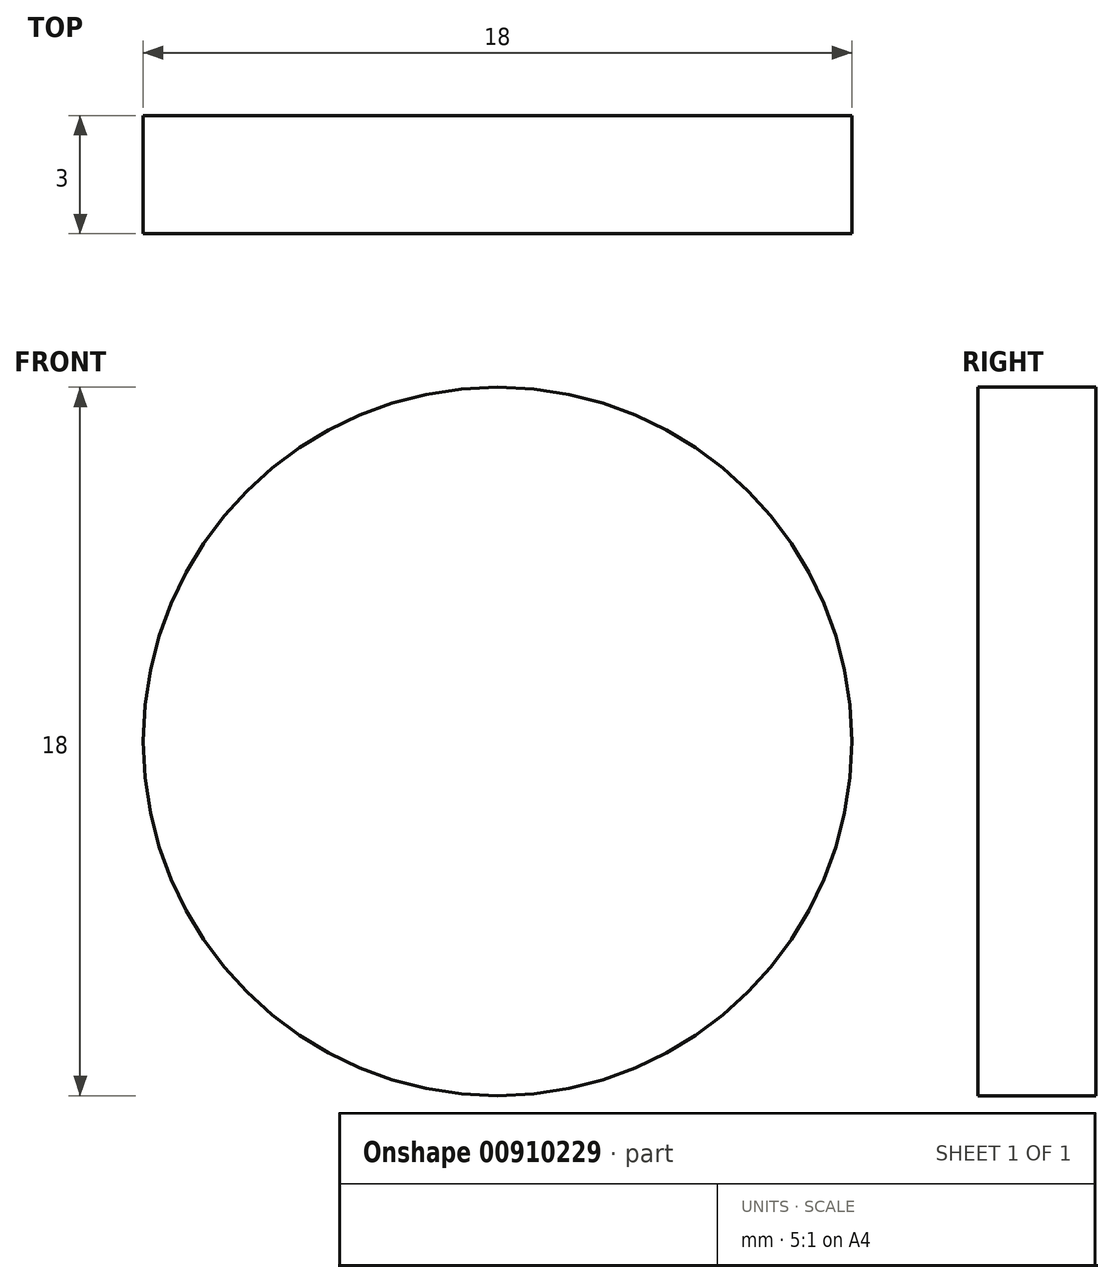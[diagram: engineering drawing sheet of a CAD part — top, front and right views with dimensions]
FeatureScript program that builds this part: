
annotation { "Feature Type Name" : "Feature", "Feature Type Description" : "" }
export const myFeature = defineFeature(function(context is Context, id is Id, definition is map)
    precondition{}
    {
        {
            var Q0;
            Q0=qCreatedBy(makeId("Front.planeOp"),FACE);
            var sketch = newSketch(context, id + "F0", { "sketchPlane" : qUnion([Q0])});
            skCircle(sketch, "E0", {"center": v(0, 0) * mm, "radius": 9 * mm});
            skCircle(sketch, "E1", {"center": v(0, 0) * mm, "radius": 7 * mm});
            skSolve(sketch);
        }
        {
            var Q0;
            Q0 = qSketchRegion(id + "F0", true);
            var Q1;
            Q1=makeQuery(id+"F0.imprint","IMPRINT",FACE,{"disambiguationData":[TD([[makeQuery(id+"F0.imprint","IMPRINT",EDGE,{"derivedFrom":sQuery(id+"F0.wireOp",EDGE,"E1")}),1.0]])]});
            extrude(context, id + "F1", {"entities" : qUnion([Q0, Q1]), "depth" : 3 * mm, "offsetDistance" : 25 * mm});
        }
        {
            var Q0;
            Q0=sQuery(id+"F0.wireOp",EDGE,"E1");
            extrude(context, id + "F2", {"bodyType" : ToolBodyType.SURFACE, "surfaceEntities" : qUnion([Q0]), "depth" : 27 * mm, "offsetDistance" : 25 * mm});
        }
    });
